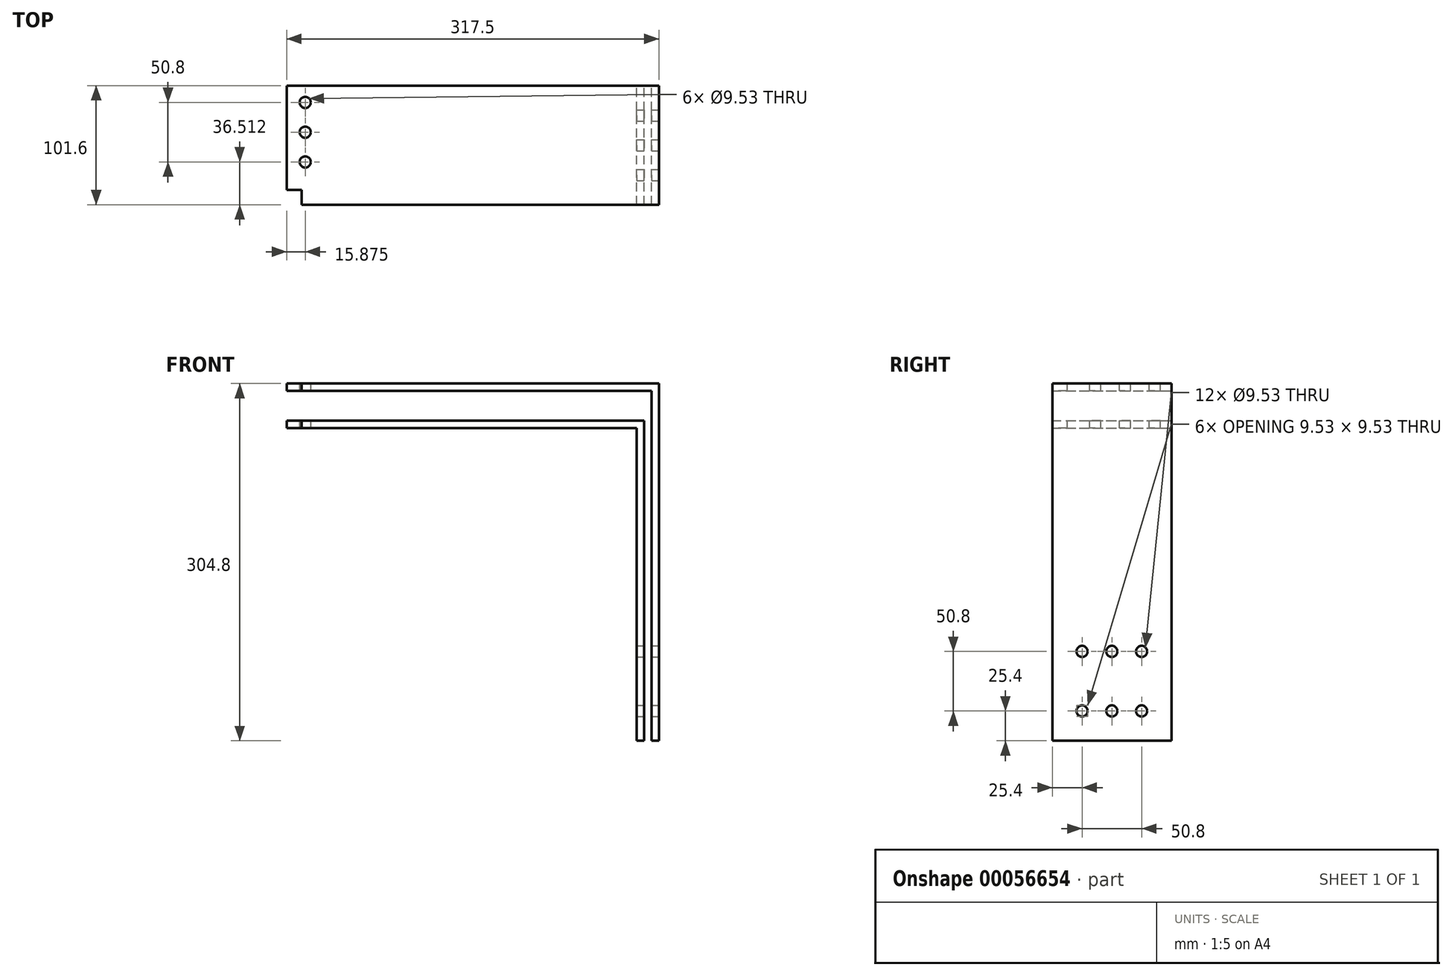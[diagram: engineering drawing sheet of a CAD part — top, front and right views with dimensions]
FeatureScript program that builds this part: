
annotation { "Feature Type Name" : "Feature", "Feature Type Description" : "" }
export const myFeature = defineFeature(function(context is Context, id is Id, definition is map)
    precondition{}
    {
        {
            var Q0;
            Q0=qCreatedBy(makeId("Front.planeOp"),FACE);
            var sketch = newSketch(context, id + "F0", { "sketchPlane" : qUnion([Q0])});
            skLineSegment(sketch, "E0", {"start": v(0, -31.75) * mm, "end": v(304.8, -31.75) * mm});
            skLineSegment(sketch, "E1", {"start": v(304.8, -31.75) * mm, "end": v(304.8, -304.8) * mm});
            skLineSegment(sketch, "E2", {"start": v(298.45, -38.1) * mm, "end": v(0, -38.1) * mm});
            skLineSegment(sketch, "E3", {"start": v(311.15, -6.35) * mm, "end": v(0, -6.35) * mm});
            skLineSegment(sketch, "E4", {"start": v(0, -6.35) * mm, "end": v(0, 0) * mm});
            skLineSegment(sketch, "E5", {"start": v(0, 0) * mm, "end": v(317.5, 0) * mm});
            skLineSegment(sketch, "E6", {"start": v(317.5, 0) * mm, "end": v(317.5, -304.8) * mm});
            skLineSegment(sketch, "E7", {"start": v(298.45, -304.8) * mm, "end": v(304.8, -304.8) * mm});
            skLineSegment(sketch, "E8.trimOffspring", {"start": v(298.45, -304.8) * mm, "end": v(298.45, -38.1) * mm});
            skLineSegment(sketch, "E9.trimOffspring", {"start": v(311.15, -304.8) * mm, "end": v(311.15, -6.35) * mm});
            skLineSegment(sketch, "E10.trimOffspring", {"start": v(311.15, -304.8) * mm, "end": v(317.5, -304.8) * mm});
            skLineSegment(sketch, "E11", {"start": v(0, -31.75) * mm, "end": v(0, -38.1) * mm});
            skSolve(sketch);
        }
        {
            var Q0;
            Q0=qSketchRegion(id+"F0",true);
            extrude(context, id + "F1", {"entities" : qUnion([Q0]), "endBound" : BoundingType.SYMMETRIC, "depth" : 101.6 * mm});
        }
        {
            var Q0;
            Q0=makeQuery(id+"F1.opExtrude","SWEPT_FACE",FACE,{"disambiguationData":[OSD([sQuery(id+"F0.wireOp",EDGE,"E6")])]});
            var sketch = newSketch(context, id + "F2", { "sketchPlane" : qUnion([Q0])});
            skCircle(sketch, "E12", {"center": v(-25.4, -279.4) * mm, "radius": 4.76 * mm});
            skCircle(sketch, "E13.0.1.0", {"center": v(-25.4, -228.6) * mm, "radius": 4.76 * mm});
            skCircle(sketch, "E13.1.0.0", {"center": v(0, -279.4) * mm, "radius": 4.76 * mm});
            skCircle(sketch, "E13.1.1.0", {"center": v(0, -228.6) * mm, "radius": 4.76 * mm});
            skCircle(sketch, "E13.2.0.0", {"center": v(25.4, -279.4) * mm, "radius": 4.76 * mm});
            skCircle(sketch, "E13.2.1.0", {"center": v(25.4, -228.6) * mm, "radius": 4.76 * mm});
            skLineSegment(sketch, "E13.direction1", {"start": v(-25.4, -279.4) * mm, "end": v(0, -279.4) * mm, "construction": true});
            skLineSegment(sketch, "E13.direction2", {"start": v(-25.4, -279.4) * mm, "end": v(-25.4, -228.6) * mm, "construction": true});
            skSolve(sketch);
        }
        {
            var Q0;
            Q0=qSketchRegion(id+"F2",true);
            extrude(context, id + "F3", {"entities" : qUnion([Q0]), "operationType" : NewBodyOperationType.REMOVE, "endBound" : BoundingType.THROUGH_ALL, "oppositeDirection" : true, "depth" : 25.4 * mm});
        }
        {
            var Q0;
            Q0=makeQuery(id+"F1.opExtrude","SWEPT_FACE",FACE,{"disambiguationData":[OSD([sQuery(id+"F0.wireOp",EDGE,"E5")])]});
            var sketch = newSketch(context, id + "F4", { "sketchPlane" : qUnion([Q0])});
            skCircle(sketch, "E14", {"center": v(15.88, -14.29) * mm, "radius": 4.76 * mm});
            skCircle(sketch, "E15.0.1.0", {"center": v(15.88, 11.11) * mm, "radius": 4.76 * mm});
            skCircle(sketch, "E15.0.2.0", {"center": v(15.88, 36.51) * mm, "radius": 4.76 * mm});
            skLineSegment(sketch, "E15.direction1", {"start": v(-97.7, -14.29) * mm, "end": v(15.88, -14.29) * mm, "construction": true});
            skLineSegment(sketch, "E15.direction2", {"start": v(15.88, -14.29) * mm, "end": v(15.88, 11.11) * mm, "construction": true});
            skLineSegment(sketch, "E16.bottom", {"start": v(0, -50.8) * mm, "end": v(12.7, -50.8) * mm});
            skLineSegment(sketch, "E16.top", {"start": v(0, -38.1) * mm, "end": v(12.7, -38.1) * mm});
            skLineSegment(sketch, "E16.left", {"start": v(0, -50.8) * mm, "end": v(0, -38.1) * mm});
            skLineSegment(sketch, "E16.right", {"start": v(12.7, -50.8) * mm, "end": v(12.7, -38.1) * mm});
            skSolve(sketch);
        }
        {
            var Q0;
            Q0=qSketchRegion(id+"F4",true);
            extrude(context, id + "F5", {"entities" : qUnion([Q0]), "operationType" : NewBodyOperationType.REMOVE, "endBound" : BoundingType.THROUGH_ALL, "oppositeDirection" : true, "depth" : 25.4 * mm});
        }
    });
